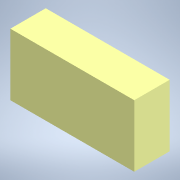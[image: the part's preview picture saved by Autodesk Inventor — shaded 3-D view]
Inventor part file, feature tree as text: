
AUTODESK INVENTOR PART (.ipt)
format: ipt  version: 2022.3 (Build 263350000, 350)  size: 96,768 bytes
history: native  units: in
note: dims shown in document units (in); Inventor stores cm internally (conversion verified against a paired STEP export)
features: extrude x1, sketch x1
ambient origin geometry x8: Origin, YZ Plane, XZ Plane, XY Plane, X Axis, Y Axis, Z Axis, Center Point
bodies: Solid1 (feature_tree)
feature tree (2):
  extrude  "Extrusion1"  Depth=7.0in
  sketch  "Sketch1"  dims[d0=2.0in d1=7.0in d2=3.5in d3=0.0in]
